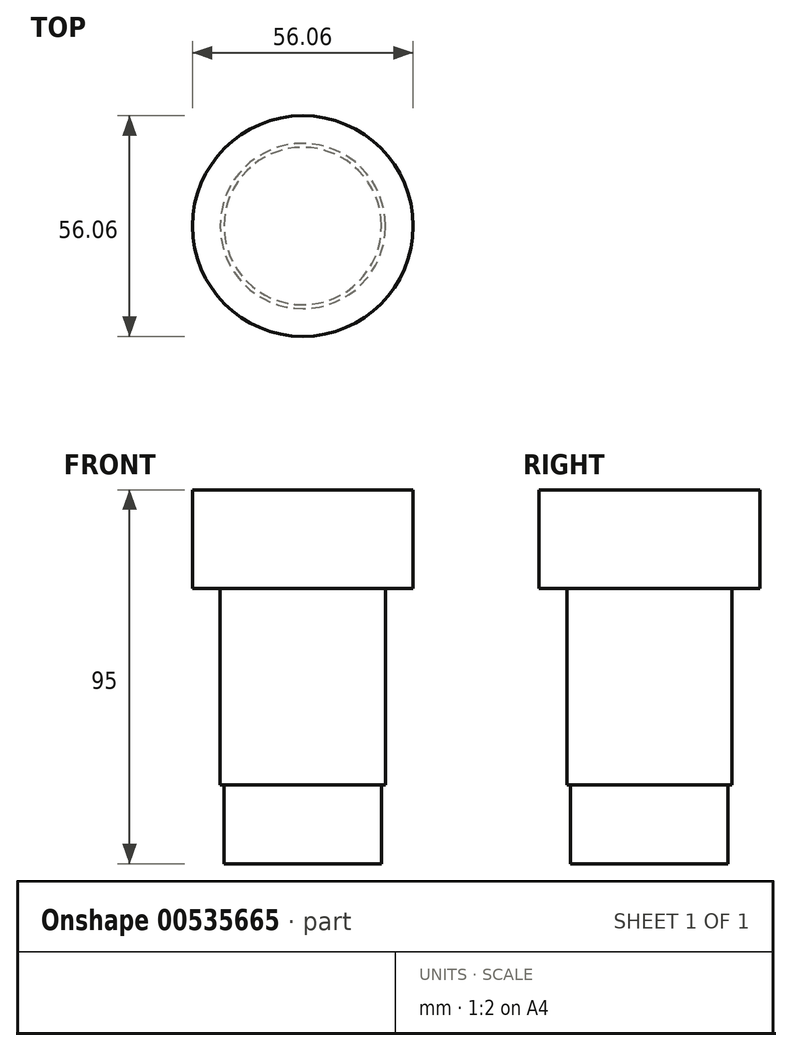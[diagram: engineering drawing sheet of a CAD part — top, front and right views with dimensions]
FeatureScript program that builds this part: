
annotation { "Feature Type Name" : "Feature", "Feature Type Description" : "" }
export const myFeature = defineFeature(function(context is Context, id is Id, definition is map)
    precondition{}
    {
        {
            var Q0;
            Q0=qCreatedBy(makeId("Top.planeOp"),FACE);
            var sketch = newSketch(context, id + "F0", { "sketchPlane" : qUnion([Q0])});
            skCircle(sketch, "E0", {"center": v(0, 0) * mm, "radius": 21 * mm});
            skCircle(sketch, "E1", {"center": v(0, 0) * mm, "radius": 20 * mm});
            skSolve(sketch);
        }
        {
            var Q0;
            Q0=makeQuery(id+"F0.imprint","IMPRINT",FACE,{"disambiguationData":[TD([[makeQuery(id+"F0.imprint","IMPRINT",EDGE,{"derivedFrom":sQuery(id+"F0.wireOp",EDGE,"E0")}),1.0]])]});
            extrude(context, id + "F1", {"entities" : qUnion([Q0]), "depth" : 50 * mm, "offsetDistance" : 25 * mm});
        }
        {
            var Q0;
            Q0=makeQuery(id+"F1.opExtrude","CAP_FACE",FACE,{"disambiguationData":[OSD([sQuery(id+"F0.wireOp",EDGE,"E0"),sQuery(id+"F0.wireOp",EDGE,"E1")])],"isStart":false});
            var sketch = newSketch(context, id + "F2", { "sketchPlane" : qUnion([Q0])});
            skCircle(sketch, "E2.0", {"center": v(0, 0) * mm, "radius": 21 * mm});
            skCircle(sketch, "E3.0", {"center": v(0, 0) * mm, "radius": 20 * mm});
            skCircle(sketch, "E4", {"center": v(0, 0) * mm, "radius": 28.03 * mm});
            skSolve(sketch);
        }
        {
            var Q0;
            Q0=makeQuery(id+"F2.imprint","IMPRINT",FACE,{"disambiguationData":[TD([[makeQuery(id+"F2.imprint","IMPRINT",EDGE,{"derivedFrom":sQuery(id+"F2.wireOp",EDGE,"E3.0")}),1.0]])]});
            extrude(context, id + "F3", {"entities" : qUnion([Q0]), "oppositeDirection" : true, "depth" : 70 * mm, "offsetDistance" : 25 * mm});
        }
        {
            var Q0;
            Q0=makeQuery(id+"F2.imprint","IMPRINT",FACE,{"disambiguationData":[TD([[makeQuery(id+"F2.imprint","IMPRINT",EDGE,{"derivedFrom":sQuery(id+"F2.wireOp",EDGE,"E3.0")}),1.0]])]});
            var Q1;
            Q1=makeQuery(id+"F2.imprint","IMPRINT",FACE,{"disambiguationData":[TD([[makeQuery(id+"F2.imprint","IMPRINT",EDGE,{"derivedFrom":sQuery(id+"F2.wireOp",EDGE,"E2.0")}),1.0]])]});
            var Q2;
            Q2=makeQuery(id+"F2.imprint","IMPRINT",FACE,{"disambiguationData":[TD([[makeQuery(id+"F2.imprint","IMPRINT",EDGE,{"derivedFrom":sQuery(id+"F2.wireOp",EDGE,"E2.0")}),-1.0]])]});
            extrude(context, id + "F4", {"entities" : qUnion([Q0, Q1, Q2]), "operationType" : NewBodyOperationType.ADD, "depth" : 25 * mm, "offsetDistance" : 25 * mm});
        }
    });
